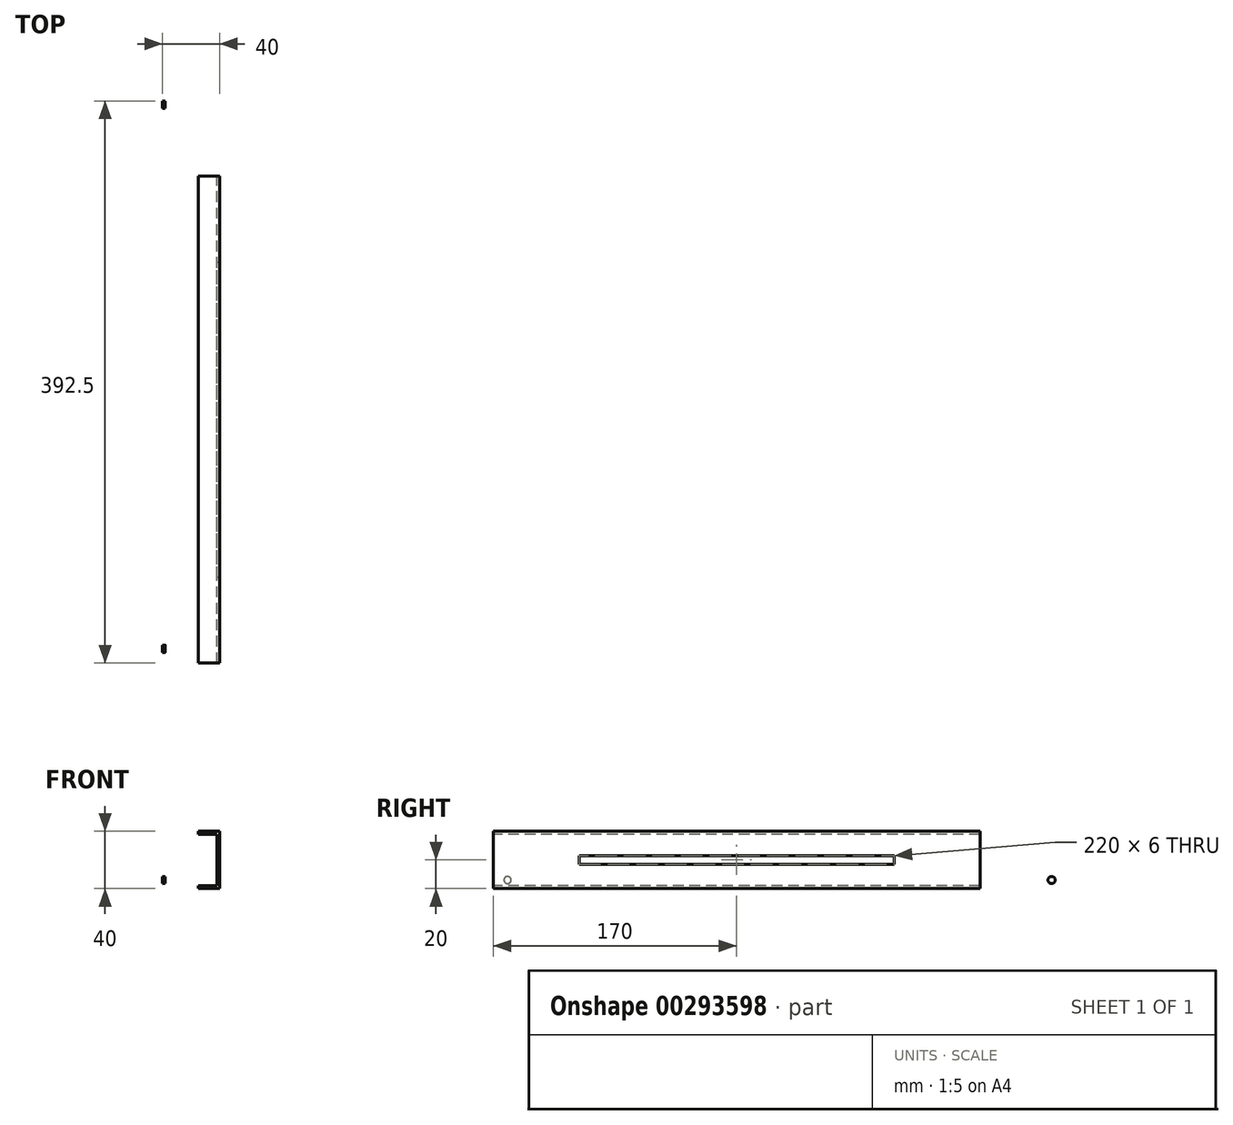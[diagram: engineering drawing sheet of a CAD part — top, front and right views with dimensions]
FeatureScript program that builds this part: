
annotation { "Feature Type Name" : "Feature", "Feature Type Description" : "" }
export const myFeature = defineFeature(function(context is Context, id is Id, definition is map)
    precondition{}
    {
        {
            var Q0;
            Q0=qCreatedBy(makeId("Front.planeOp"),FACE);
            var sketch = newSketch(context, id + "F0", { "sketchPlane" : qUnion([Q0])});
            skLineSegment(sketch, "E0.bottom", {"start": v(-20, 20) * mm, "end": v(20, 20) * mm});
            skLineSegment(sketch, "E0.top", {"start": v(-20, -20) * mm, "end": v(20, -20) * mm});
            skLineSegment(sketch, "E0.left", {"start": v(-20, 20) * mm, "end": v(-20, -20) * mm});
            skLineSegment(sketch, "E0.right", {"start": v(20, 20) * mm, "end": v(20, -20) * mm});
            skPoint(sketch, "E0.middle", {"position": v(0, 0) * mm});
            skLineSegment(sketch, "E1.0", {"start": v(-18, 18) * mm, "end": v(18, 18) * mm});
            skLineSegment(sketch, "E1.1", {"start": v(-18, 18) * mm, "end": v(-18, -18) * mm});
            skLineSegment(sketch, "E1.2", {"start": v(-18, -18) * mm, "end": v(18, -18) * mm});
            skLineSegment(sketch, "E1.3", {"start": v(18, 18) * mm, "end": v(18, -18) * mm});
            skSolve(sketch);
        }
        {
            var Q0;
            Q0=makeQuery(id+"F0.imprint","IMPRINT",FACE,{"disambiguationData":[TD([[makeQuery(id+"F0.imprint","IMPRINT",EDGE,{"derivedFrom":sQuery(id+"F0.wireOp",EDGE,"E0.bottom")}),-1.0]])]});
            extrude(context, id + "F1", {"entities" : qUnion([Q0]), "depth" : 400 * mm});
        }
        {
            var Q0;
            Q0=makeQuery(id+"F1.opExtrude","SWEPT_FACE",FACE,{"disambiguationData":[OSD([sQuery(id+"F0.wireOp",EDGE,"E0.right")])]});
            var sketch = newSketch(context, id + "F2", { "sketchPlane" : qUnion([Q0])});
            skLineSegment(sketch, "E2", {"start": v(-400, 0) * mm, "end": v(0, 0) * mm, "construction": true});
            skLineSegment(sketch, "E3", {"start": v(0, 0) * mm, "end": v(-230, 0) * mm, "construction": true});
            skLineSegment(sketch, "E4.bottom", {"start": v(-340, 3) * mm, "end": v(-120, 3) * mm});
            skLineSegment(sketch, "E4.top", {"start": v(-340, -3) * mm, "end": v(-120, -3) * mm});
            skLineSegment(sketch, "E4.left", {"start": v(-340, 3) * mm, "end": v(-340, -3) * mm});
            skLineSegment(sketch, "E4.right", {"start": v(-120, 3) * mm, "end": v(-120, -3) * mm});
            skPoint(sketch, "E4.middle", {"position": v(-230, 0) * mm});
            skSolve(sketch);
        }
        {
            var Q0;
            Q0=makeQuery(id+"F2.imprint","IMPRINT",FACE,{"disambiguationData":[TD([[makeQuery(id+"F2.imprint","IMPRINT",EDGE,{"derivedFrom":sQuery(id+"F2.wireOp",EDGE,"E4.bottom")}),-1.0]])]});
            extrude(context, id + "F3", {"entities" : qUnion([Q0]), "operationType" : NewBodyOperationType.REMOVE, "oppositeDirection" : true, "depth" : 2 * mm});
        }
        {
            var Q0;
            Q0=qCreatedBy(makeId("Front.planeOp"),FACE);
            var sketch = newSketch(context, id + "F4", { "sketchPlane" : qUnion([Q0])});
            skLineSegment(sketch, "E5", {"start": v(-5, -20) * mm, "end": v(-5, -18) * mm});
            skLineSegment(sketch, "E6.0", {"start": v(-20, -20) * mm, "end": v(20, -20) * mm});
            skLineSegment(sketch, "E7.0", {"start": v(-20, 20) * mm, "end": v(20, 20) * mm});
            skLineSegment(sketch, "E8.0", {"start": v(-18, -18) * mm, "end": v(18, -18) * mm});
            skLineSegment(sketch, "E9.0", {"start": v(-18, 18) * mm, "end": v(18, 18) * mm});
            skLineSegment(sketch, "E10.trimOffspring", {"start": v(-5, 18) * mm, "end": v(-5, 20) * mm});
            skLineSegment(sketch, "E11.0", {"start": v(-20, 20) * mm, "end": v(-20, -20) * mm});
            skLineSegment(sketch, "E12.0", {"start": v(20, 20) * mm, "end": v(20, -20) * mm});
            skLineSegment(sketch, "E13.0", {"start": v(18, 18) * mm, "end": v(18, -18) * mm});
            skLineSegment(sketch, "E14.0", {"start": v(-18, 18) * mm, "end": v(-18, -18) * mm});
            skSolve(sketch);
        }
        {
            var Q0;
            {var subQ1=sQuery(id+"F4.wireOp",EDGE,"E5");Q0=makeQuery(id+"F4.imprint","IMPRINT",FACE,{"disambiguationData":[TD([[makeQuery(id+"F4.imprint","IMPRINT",EDGE,{"derivedFrom":subQ1}),-1.0]])]});}
            extrude(context, id + "F5", {"entities" : qUnion([Q0]), "operationType" : NewBodyOperationType.REMOVE, "depth" : 60 * mm});
        }
        {
            var Q0;
            Q0=makeQuery(id+"F1.opExtrude","SWEPT_FACE",FACE,{"disambiguationData":[OSD([sQuery(id+"F0.wireOp",EDGE,"E0.left")])]});
            var sketch = newSketch(context, id + "F6", { "sketchPlane" : qUnion([Q0])});
            skLineSegment(sketch, "E15", {"start": v(0, 0) * mm, "end": v(404.3, 0) * mm, "construction": true});
            skPoint(sketch, "E15.endSnap0", {"position": v(400, 0) * mm});
            skCircle(sketch, "E16", {"center": v(10, 14) * mm, "radius": 2.5 * mm});
            skCircle(sketch, "E17", {"center": v(390, 14) * mm, "radius": 2.5 * mm});
            skCircle(sketch, "E18.MirrorC", {"center": v(390, -14) * mm, "radius": 2.5 * mm});
            skCircle(sketch, "E19.MirrorC", {"center": v(10, -14) * mm, "radius": 2.5 * mm});
            skSolve(sketch);
        }
        {
            var Q0;
            Q0=makeQuery(id+"F6.imprint","IMPRINT",FACE,{"disambiguationData":[TD([[makeQuery(id+"F6.imprint","IMPRINT",EDGE,{"derivedFrom":sQuery(id+"F6.wireOp",EDGE,"E16")}),1.0]])]});
            var Q1;
            Q1=makeQuery(id+"F6.imprint","IMPRINT",FACE,{"disambiguationData":[TD([[makeQuery(id+"F6.imprint","IMPRINT",EDGE,{"derivedFrom":sQuery(id+"F6.wireOp",EDGE,"E19.MirrorC")}),-1.0]])]});
            var Q2;
            Q2=makeQuery(id+"F6.imprint","IMPRINT",FACE,{"disambiguationData":[TD([[makeQuery(id+"F6.imprint","IMPRINT",EDGE,{"derivedFrom":sQuery(id+"F6.wireOp",EDGE,"E17")}),1.0]])]});
            var Q3;
            Q3=makeQuery(id+"F6.imprint","IMPRINT",FACE,{"disambiguationData":[TD([[makeQuery(id+"F6.imprint","IMPRINT",EDGE,{"derivedFrom":sQuery(id+"F6.wireOp",EDGE,"E18.MirrorC")}),-1.0]])]});
            extrude(context, id + "F7", {"entities" : qUnion([Q0, Q1, Q2, Q3]), "operationType" : NewBodyOperationType.REMOVE, "oppositeDirection" : true, "depth" : 25 * mm});
        }
    });
